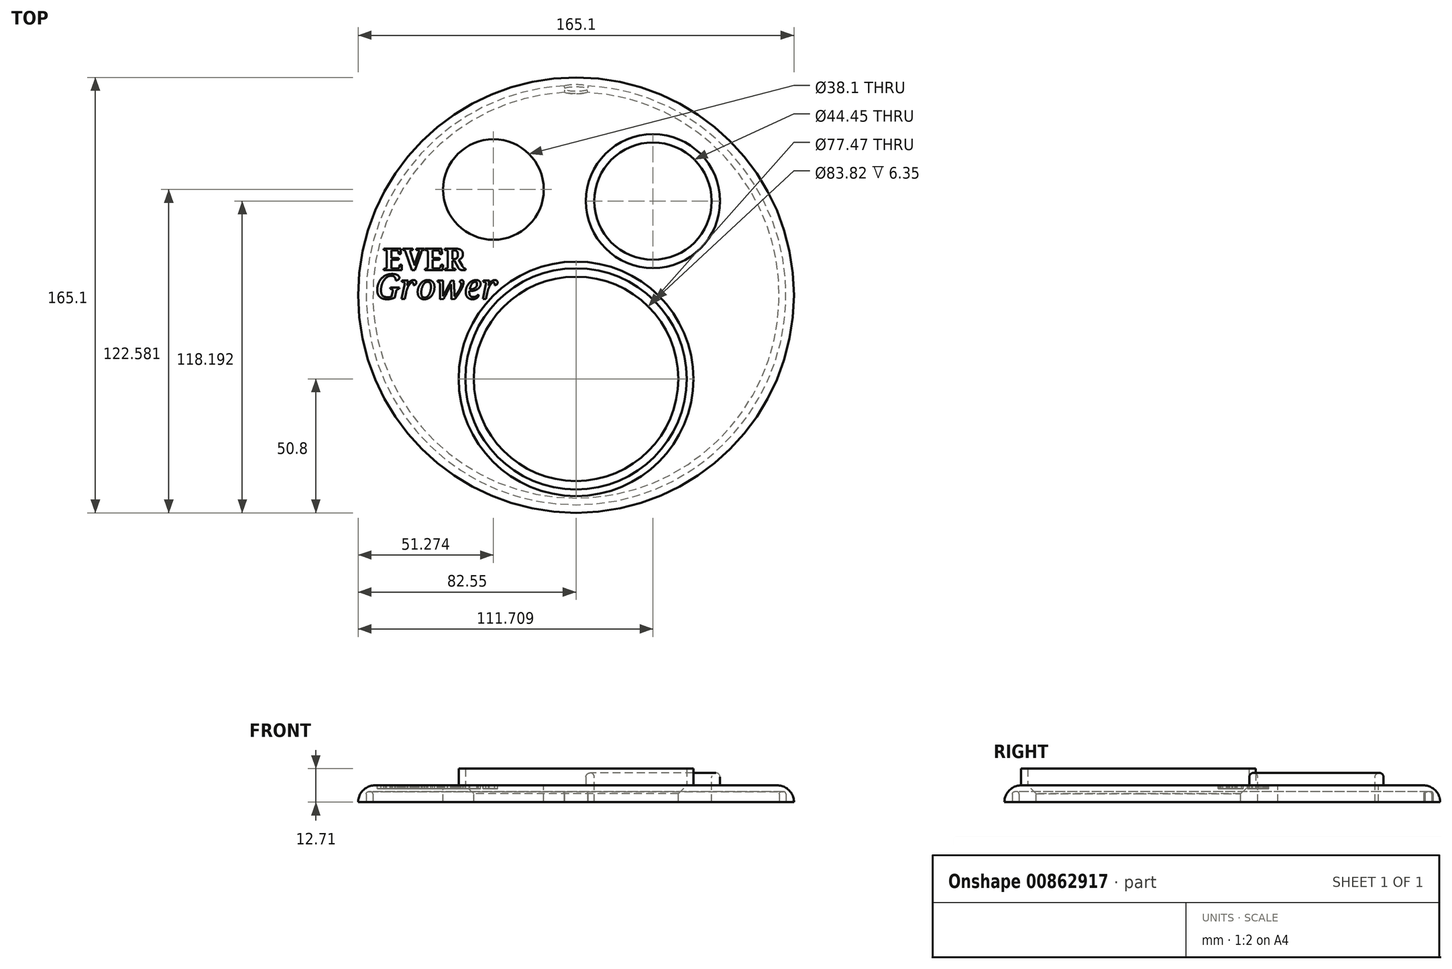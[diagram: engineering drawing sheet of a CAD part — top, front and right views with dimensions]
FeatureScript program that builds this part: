
annotation { "Feature Type Name" : "Feature", "Feature Type Description" : "" }
export const myFeature = defineFeature(function(context is Context, id is Id, definition is map)
    precondition{}
    {
        {
            var Q0;
            Q0=qCreatedBy(makeId("Top.planeOp"),FACE);
            var sketch = newSketch(context, id + "F0", { "sketchPlane" : qUnion([Q0])});
            skLineSegment(sketch, "E0", {"start": v(0, 0) * mm, "end": v(-82.55, 0) * mm});
            skCircle(sketch, "E1", {"center": v(0, 0) * mm, "radius": 82.55 * mm});
            skSolve(sketch);
        }
        {
            var Q0;
            Q0=makeQuery(id+"F0.imprint","IMPRINT",FACE,{"disambiguationData":[TD([[makeQuery(id+"F0.imprint","IMPRINT",EDGE,{"derivedFrom":sQuery(id+"F0.wireOp",EDGE,"E1")}),1.0]])]});
            extrude(context, id + "F1", {"entities" : qUnion([Q0]), "endBound" : BoundingType.SYMMETRIC, "depth" : 6.35 * mm, "offsetDistance" : 25.4 * mm});
        }
        {
            var Q0;
            Q0=makeQuery(id+"F1.opExtrude","CAP_FACE",FACE,{"disambiguationData":[OSD([sQuery(id+"F0.wireOp",EDGE,"E1")])],"isStart":false});
            fillet(context, id + "F2", {"entities" : qUnion([Q0]), "radius" : 6.35 * mm, "tangentPropagation" : true, "allowEdgeOverflow" : false});
        }
        {
            var Q0;
            Q0=makeQuery(id+"F1.opExtrude","CAP_FACE",FACE,{"disambiguationData":[OSD([sQuery(id+"F0.wireOp",EDGE,"E1")])],"isStart":true});
            var sketch = newSketch(context, id + "F3", { "sketchPlane" : qUnion([Q0])});
            skLineSegment(sketch, "E2", {"start": v(0, 0) * mm, "end": v(0, -79.4) * mm, "construction": true});
            skLineSegment(sketch, "E3", {"start": v(0, 0) * mm, "end": v(0, -77.11) * mm, "construction": true});
            skLineSegment(sketch, "E4", {"start": v(0, -77.11) * mm, "end": v(0, -79.4) * mm, "construction": true});
            skLineSegment(sketch, "E5", {"start": v(0, -79.4) * mm, "end": v(0, -78.13) * mm, "construction": true});
            skLineSegment(sketch, "E6", {"start": v(0, -78.13) * mm, "end": v(6.35, -78.13) * mm, "construction": true});
            skLineSegment(sketch, "E7", {"start": v(0, -78.13) * mm, "end": v(0, -79.9) * mm, "construction": true});
            skEllipse(sketch, "E8", {"center": v(0, -78.13) * mm, "majorRadius": 6.35 * mm, "minorRadius": 1.78 * mm, "majorAxis": v(1, 0)});
            skCircle(sketch, "E9", {"center": v(0, 0) * mm, "radius": 79.5 * mm});
            skLineSegment(sketch, "E10", {"start": v(0, 0) * mm, "end": v(-79.5, 0) * mm, "construction": true});
            skCircle(sketch, "E11", {"center": v(0, 0) * mm, "radius": 76.96 * mm});
            skLineSegment(sketch, "E12", {"start": v(0, 0) * mm, "end": v(76.96, 0) * mm, "construction": true});
            skSolve(sketch);
        }
        {
            var Q0;
            Q0=makeQuery(id+"F1.opExtrude","CAP_FACE",FACE,{"disambiguationData":[OSD([sQuery(id+"F0.wireOp",EDGE,"E1")])],"isStart":false});
            var sketch = newSketch(context, id + "F4", { "sketchPlane" : qUnion([Q0])});
            skLineSegment(sketch, "E13", {"start": v(0, 0) * mm, "end": v(0, -69.85) * mm, "construction": true});
            skLineSegment(sketch, "E14", {"start": v(0, -69.85) * mm, "end": v(0, -31.75) * mm, "construction": true});
            skCircle(sketch, "E15", {"center": v(0, -31.75) * mm, "radius": 38.6 * mm});
            skSolve(sketch);
        }
        {
            var Q0;
            Q0=makeQuery(id+"F1.opExtrude","CAP_FACE",FACE,{"disambiguationData":[OSD([sQuery(id+"F0.wireOp",EDGE,"E1")])],"isStart":false});
            var sketch = newSketch(context, id + "F5", { "sketchPlane" : qUnion([Q0])});
            skLineSegment(sketch, "E16", {"start": v(0, 0) * mm, "end": v(0, 73.03) * mm, "construction": true});
            skLineSegment(sketch, "E17", {"start": v(0, 0) * mm, "end": v(-73.03, 0) * mm, "construction": true});
            skLineSegment(sketch, "E18", {"start": v(0, 0) * mm, "end": v(-44.96, 57.54) * mm, "construction": true});
            skLineSegment(sketch, "E19", {"start": v(-44.96, 57.54) * mm, "end": v(-31.28, 40.03) * mm, "construction": true});
            skSolve(sketch);
        }
        {
            var Q0;
            Q0=sQuery(id+"F5.wireOp",VERTEX,"E19.end");
            var Q1;
            Q1=makeQuery(id+"F1.opExtrude","SWEPT_BODY",BODY,{"disambiguationData":[OSD([sQuery(id+"F0.wireOp",EDGE,"E1")])]});
            hole(context, id + "F6", {"style" : HoleStyle.SIMPLE, "endStyle" : HoleEndStyle.THROUGH, "holeDiameter" : 38.1 * mm, "majorDiameter" : 6.35 * mm, "isTappedThrough" : true, "tappedDepth" : 12.7 * mm, "tapClearance" : 3, "startFromSketch" : true, "locations" : qUnion([Q0]), "scope" : qUnion([Q1])});
        }
        {
            var Q0;
            {var subQ75=sQuery(id+"F0.wireOp",EDGE,"E1");var subQ76=makeQuery(id+"F2.opFillet","BLEND_FACE",FACE,{"disambiguationData":[OSD([subQ75])]});Q0=makeQuery(id+"FSR7zYV3hxNYAOb_1.boolean.opBoolean","SPLIT",FACE,{"disambiguationData":[TD([subQ76])],"derivedFrom":makeQuery(id+"FO9AwFJfpJHEqtB_1.boolean.opBoolean","SPLIT",FACE,{"disambiguationData":[TD([subQ76])],"derivedFrom":makeQuery(id+"F1.opExtrude","CAP_FACE",FACE,{"disambiguationData":[OSD([subQ75])],"isStart":false})})});}
            var sketch = newSketch(context, id + "F7", { "sketchPlane" : qUnion([Q0])});
            skCircle(sketch, "E20", {"center": v(0, -31.75) * mm, "radius": 46.35 * mm, "construction": true});
            skCircle(sketch, "E21", {"center": v(0, 0) * mm, "radius": 73.03 * mm, "construction": true});
            skCircle(sketch, "E22", {"center": v(29.16, 35.64) * mm, "radius": 22.23 * mm});
            skCircle(sketch, "E23", {"center": v(29.16, 35.64) * mm, "radius": 25.4 * mm});
            skLineSegment(sketch, "E24", {"start": v(0, 0) * mm, "end": v(29.16, 35.64) * mm, "construction": true});
            skLineSegment(sketch, "E25", {"start": v(0, 0) * mm, "end": v(0, 35.64) * mm, "construction": true});
            skLineSegment(sketch, "E26", {"start": v(0, 35.64) * mm, "end": v(29.16, 35.64) * mm, "construction": true});
            skSolve(sketch);
        }
        {
            var Q0;
            Q0=sQuery(id+"F7.wireOp",VERTEX,"E24.end");
            var Q1;
            Q1=makeQuery(id+"F1.opExtrude","SWEPT_BODY",BODY,{"disambiguationData":[OSD([sQuery(id+"F0.wireOp",EDGE,"E1")])]});
            hole(context, id + "F8", {"style" : HoleStyle.SIMPLE, "endStyle" : HoleEndStyle.THROUGH, "holeDiameter" : 44.45 * mm, "majorDiameter" : 6.35 * mm, "isTappedThrough" : true, "tappedDepth" : 12.7 * mm, "tapClearance" : 3, "startFromSketch" : true, "locations" : qUnion([Q0]), "scope" : qUnion([Q1])});
        }
        {
            var Q0;
            Q0 = qSketchRegion(id + "F7", true);
            extrude(context, id + "F9", {"entities" : qUnion([Q0]), "operationType" : NewBodyOperationType.ADD, "depth" : 4.76 * mm, "offsetDistance" : 25.4 * mm});
        }
        {
            var Q0;
            Q0=makeQuery(id+"F9.opExtrude","CAP_FACE",FACE,{"disambiguationData":[OSD([sQuery(id+"F7.wireOp",EDGE,"E22"),sQuery(id+"F7.wireOp",EDGE,"E23")])],"isStart":false});
            fillet(context, id + "F10", {"entities" : qUnion([Q0]), "radius" : 1.59 * mm, "tangentPropagation" : true, "allowEdgeOverflow" : false});
        }
        {
            var Q0;
            Q0=makeQuery(id+"F1.opExtrude","CAP_FACE",FACE,{"disambiguationData":[OSD([sQuery(id+"F0.wireOp",EDGE,"E1")])],"isStart":false});
            var sketch = newSketch(context, id + "F11", { "sketchPlane" : qUnion([Q0])});
            skLineSegment(sketch, "E27", {"start": v(0, 0) * mm, "end": v(0, -31.75) * mm, "construction": true});
            skCircle(sketch, "E28", {"center": v(0, -31.75) * mm, "radius": 44.45 * mm});
            skCircle(sketch, "E29", {"center": v(0, -31.75) * mm, "radius": 41.91 * mm});
            skSolve(sketch);
        }
        {
            var Q0;
            Q0=makeQuery(id+"F1.opExtrude","CAP_FACE",FACE,{"disambiguationData":[OSD([sQuery(id+"F0.wireOp",EDGE,"E1")])],"isStart":false});
            var sketch = newSketch(context, id + "F12", { "sketchPlane" : qUnion([Q0])});
            skCircle(sketch, "E30", {"center": v(-31.28, 40.03) * mm, "radius": 24.13 * mm, "construction": true});
            skLineSegment(sketch, "E31", {"start": v(-31.28, 40.03) * mm, "end": v(-31.28, 15.9) * mm, "construction": true});
            skText(sketch, "E32", { "text": "EVER", "fontName": "NotoSerif-Bold.ttf"});
            skText(sketch, "E33", { "text": "Grower", "fontName": "NotoSerif-Italic.ttf"});
            const initialGuessF12  = {"E32": [-0.07312, 0.00942, 1, 0, 0.0083], "E33": [-0.07599, -0.00145, 1, 0, 0.00941]};
            skSetInitialGuess(sketch, initialGuessF12);
            skSolve(sketch);
        }
        {
            var Q0;
            Q0 = qSketchRegion(id + "F12", true);
            extrude(context, id + "F13", {"entities" : qUnion([Q0]), "operationType" : NewBodyOperationType.REMOVE, "oppositeDirection" : true, "depth" : 1.27 * mm, "offsetDistance" : 25.4 * mm});
        }
        {
            var Q0;
            {var subQ0=sQuery(id+"F3.wireOp",EDGE,"E11");var subQ1=sQuery(id+"F3.wireOp",EDGE,"E8");var subQ2=makeQuery(id+"F3.imprint","INTERSECT",VERTEX,{"disambiguationData":[OD(0.0)],"derivedFrom":[subQ1,subQ0]});Q0=makeQuery(id+"F3.imprint","IMPRINT",FACE,{"disambiguationData":[TD([[makeQuery(id+"F3.imprint","IMPRINT",EDGE,{"disambiguationData":[TD([[subQ2,-1.0]])],"derivedFrom":subQ1}),-1.0]])]});}
            var Q1;
            {var subQ0=sQuery(id+"F3.wireOp",EDGE,"E11");var subQ1=sQuery(id+"F3.wireOp",EDGE,"E8");var subQ2=makeQuery(id+"F3.imprint","INTERSECT",VERTEX,{"disambiguationData":[OD(0.0)],"derivedFrom":[subQ1,subQ0]});Q1=makeQuery(id+"F3.imprint","IMPRINT",FACE,{"disambiguationData":[TD([[makeQuery(id+"F3.imprint","IMPRINT",EDGE,{"disambiguationData":[TD([[subQ2,1.0]])],"derivedFrom":subQ1}),1.0]])]});}
            var Q2;
            {var subQ0=sQuery(id+"F3.wireOp",EDGE,"E9");var subQ1=sQuery(id+"F3.wireOp",EDGE,"E8");var subQ2=makeQuery(id+"F3.imprint","INTERSECT",VERTEX,{"disambiguationData":[OD(0.0)],"derivedFrom":[subQ1,subQ0]});Q2=makeQuery(id+"F3.imprint","IMPRINT",FACE,{"disambiguationData":[TD([[makeQuery(id+"F3.imprint","IMPRINT",EDGE,{"disambiguationData":[TD([[subQ2,-1.0]])],"derivedFrom":subQ1}),1.0]])]});}
            var Q3;
            {var subQ0=sQuery(id+"F3.wireOp",EDGE,"E11");var subQ1=sQuery(id+"F3.wireOp",EDGE,"E8");var subQ2=makeQuery(id+"F3.imprint","INTERSECT",VERTEX,{"disambiguationData":[OD(0.0)],"derivedFrom":[subQ1,subQ0]});Q3=makeQuery(id+"F3.imprint","IMPRINT",FACE,{"disambiguationData":[TD([[makeQuery(id+"F3.imprint","IMPRINT",EDGE,{"disambiguationData":[TD([[subQ2,-1.0]])],"derivedFrom":subQ1}),1.0]])]});}
            extrude(context, id + "F14", {"entities" : qUnion([Q0, Q1, Q2, Q3]), "operationType" : NewBodyOperationType.REMOVE, "oppositeDirection" : true, "depth" : 3.97 * mm, "offsetDistance" : 25.4 * mm});
        }
        {
            var Q0;
            Q0=makeQuery(id+"F14.boolean.opBoolean","COPY",FACE,{"derivedFrom":makeQuery(id+"F14.opExtrude","CAP_FACE",FACE,{"disambiguationData":[OSD([sQuery(id+"F3.wireOp",EDGE,"E8"),sQuery(id+"F3.wireOp",EDGE,"E9"),sQuery(id+"F3.wireOp",EDGE,"E11")])],"isStart":false})});
            fillet(context, id + "F15", {"entities" : qUnion([Q0]), "tangentPropagation" : true, "radius" : 0.89 * mm, "defaultsChanged" : false, "vertexSettings" : [], "allowEdgeOverflow" : false});
        }
        {
            var Q0;
            Q0=sQuery(id+"F4.wireOp",VERTEX,"E14.end");
            var Q1;
            Q1=makeQuery(id+"F1.opExtrude","SWEPT_BODY",BODY,{"disambiguationData":[OSD([sQuery(id+"F0.wireOp",EDGE,"E1")])]});
            hole(context, id + "F16", {"style" : HoleStyle.C_SINK, "endStyle" : HoleEndStyle.THROUGH, "holeDiameter" : 77.47 * mm, "cSinkDiameter" : 83.82 * mm, "cSinkAngle" : 90 * degree, "majorDiameter" : 6.35 * mm, "isTappedThrough" : true, "tappedDepth" : 12.7 * mm, "tapClearance" : 3, "startFromSketch" : true, "locations" : qUnion([Q0]), "scope" : qUnion([Q1])});
        }
        {
            var Q0;
            Q0=makeQuery(id+"F11.imprint","IMPRINT",FACE,{"disambiguationData":[TD([[makeQuery(id+"F11.imprint","IMPRINT",EDGE,{"derivedFrom":sQuery(id+"F11.wireOp",EDGE,"E28")}),1.0]])]});
            extrude(context, id + "F17", {"entities" : qUnion([Q0]), "operationType" : NewBodyOperationType.ADD, "depth" : 6.35 * mm, "offsetDistance" : 25.4 * mm});
        }
    });
